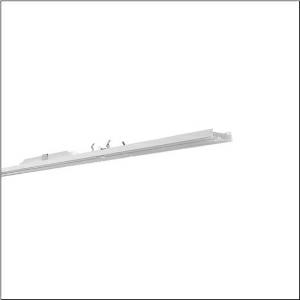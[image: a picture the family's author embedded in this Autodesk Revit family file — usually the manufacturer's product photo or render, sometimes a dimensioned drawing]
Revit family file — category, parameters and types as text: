
# Revit family: licross_r__11_recessed_mo_51ul1edv4e5f_fa7a
name_source: partatom
category: Lighting Fixtures
units: mm (PartAtom-declared; Revit-internal decimal feet)

## family parameters
Cut with Voids When Loaded = No
Host = Face
Light Source = No
Part Type = Normal
Room Calculation Point = No
Round Connector Dimension = Use Diameter
Shared = No

## types (1)
- --- (1 x LED, 14910 lm, 89.6 W, 4000K)
    Apparent Load = 90 VA
    CIE Flux Codes = 85 95 99 100 100
    Color Rendering = 80
    Color Temperature = 4000K
    Default Elevation = 1800 mm
    Description = Licross® 11 Recessed MO, luminaire insert, of sheet steel, galvanised, coil coated, white, length: 2.250mm, width: 66mm, height: 67mm, LED rated luminous flux: 14.910lm, light colour: 840, control gear: DALI 2, control gear: ECG DALI, with terminal, 5-pole, max. 2.5mm², mains connection: 230V, AC, 50/60Hz, halogen-free wiring, primary optical cover: cover, of PMMA, light emission: direct distribution, primary light characteristic: symmetric, protection rating (complete): IP40, insulation class (complete): insulation class I (protective earthing), certification: CE, ENEC, VDE, UKCA, protection symbol: D if used in an environment without relevant dust loads with corresponding accessories, permissible ambient temperature for indoor applications: -25..+35°C, corresponds to IFS (International Featured Standards) requirements for safety and quality in the food industry, reducing of maximum allowable ambient temperature of 5°C with ceiling mounting, LABS conformity tested according to VDMA 24364:2018-05, packaging unit: 1 piece
    Height = 58 mm
    Lamp = 1 x LED
    Lamp Light Flux = 14910 lm
    Lamp Power = 89.6 W
    Lamp count = 1
    Length = 2250 mm
    Luminous efficacy = 166 lm/W
    Manufacturer = Siteco
    ModVariant = No
    Model = 51UL1EDV4E5F
    Mounting Place = Ceiling
    Mounting Type = Pendant
    Number of Poles = 1
    OnlyDefault = Yes
    Power Factor = 1
    Product Name = Licross® 11 Recessed MO
    Product group = luminaire insert
    ProductGroupID = 902
    Protection Class = Protection class I
    Protection Degree = IP 40
    RLX_Detail_Level = 1
    RlxData = <blob elided: 26721 chars, md5=2091edac>
    Socket = socket
    Standby Power = 0 W
    System Light Flux = 14910 lm
    System Power = 90 W
    Type Comments = factory setting: luminous flux: 100 % | dim-lin: 254 | 400 mA
    Type Image = l_1006953.jpg
    URL = http://relux.com
    VarID = @adj_092461
    Voltage = 0 V
    Weight = 0.00 kg
    Width = 66 mm

## geometry (parser evidence)
native form markers: Blend x4, Sweep x11
no freeform markers — native parametric forms only
